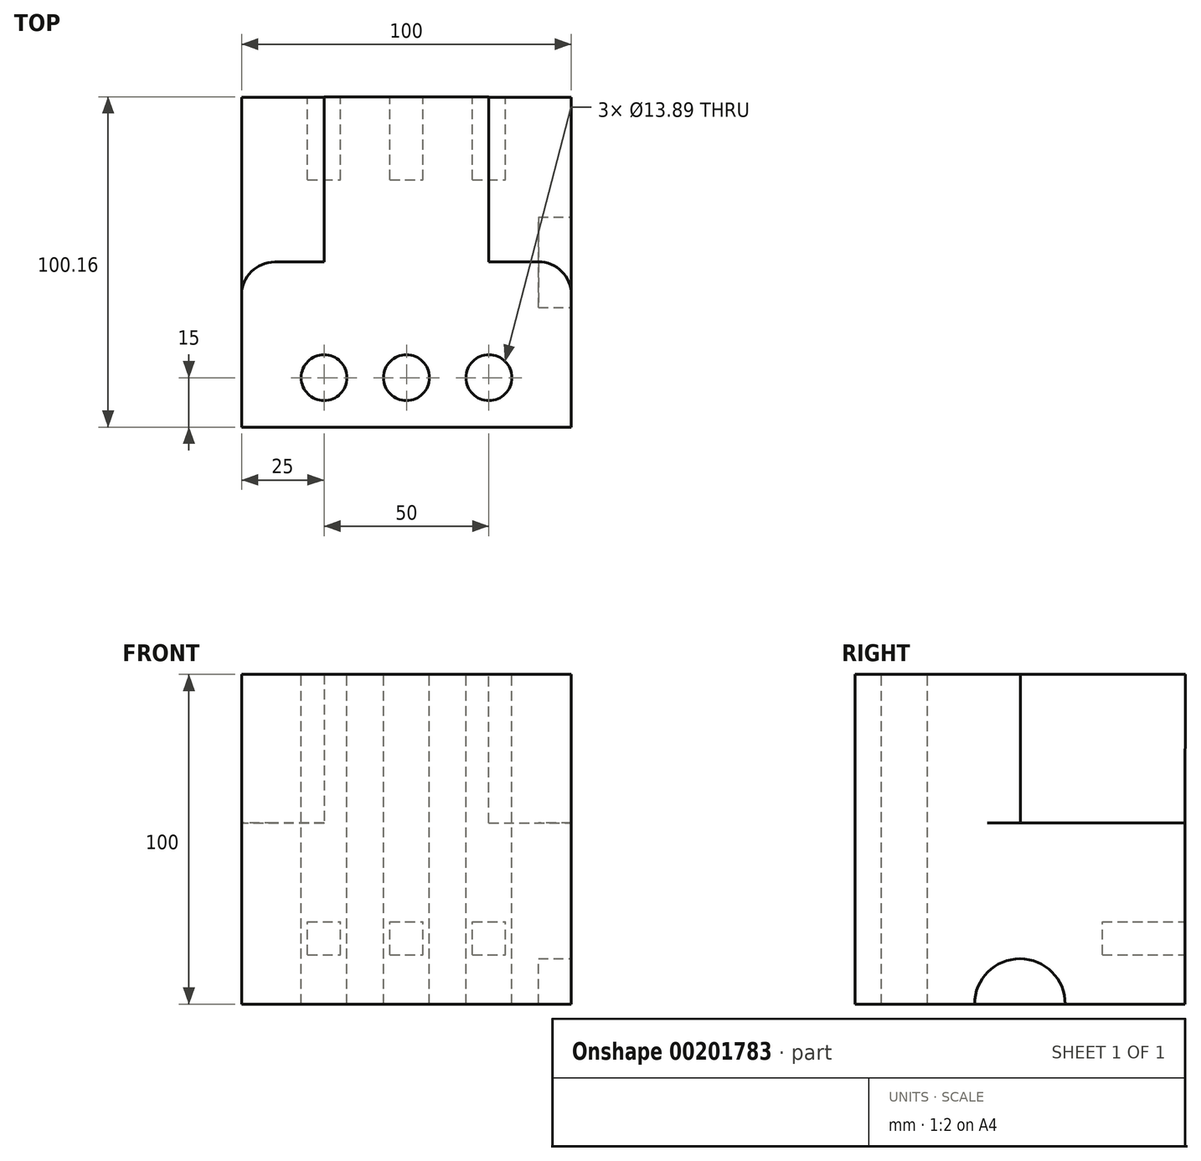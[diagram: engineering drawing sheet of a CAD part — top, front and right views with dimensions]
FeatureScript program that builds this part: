
annotation { "Feature Type Name" : "Feature", "Feature Type Description" : "" }
export const myFeature = defineFeature(function(context is Context, id is Id, definition is map)
    precondition{}
    {
        {
            var Q0;
            Q0=qCreatedBy(makeId("Right.planeOp"),FACE);
            var sketch = newSketch(context, id + "F0", { "sketchPlane" : qUnion([Q0])});
            skLineSegment(sketch, "E0", {"start": v(0, 100) * mm, "end": v(0, 0) * mm});
            skLineSegment(sketch, "E1", {"start": v(0, 0) * mm, "end": v(100, 0) * mm});
            skLineSegment(sketch, "E2", {"start": v(100, 0) * mm, "end": v(100, 55) * mm});
            skLineSegment(sketch, "E3", {"start": v(100, 55) * mm, "end": v(50, 55) * mm});
            skLineSegment(sketch, "E4", {"start": v(50, 55) * mm, "end": v(50, 100) * mm});
            skLineSegment(sketch, "E5", {"start": v(50, 100) * mm, "end": v(0, 100) * mm});
            skArc(sketch, "E6", {"start": v(63.75, 0) * mm, "mid": v(50, 13.75) * mm, "end": v(36.25, 0) * mm});
            skLineSegment(sketch, "E7", {"start": v(50, 100) * mm, "end": v(100.16, 100) * mm});
            skLineSegment(sketch, "E8", {"start": v(100, 55) * mm, "end": v(100.16, 100) * mm});
            skSolve(sketch);
        }
        {
            var Q0;
            Q0 = qSketchRegion(id + "F0", true);
            extrude(context, id + "F1", {"entities" : qUnion([Q0]), "oppositeDirection" : true, "depth" : 100 * mm});
        }
        {
            var Q0;
            {var subQ0=sQuery(id+"F0.wireOp",EDGE,"E6");Q0=makeQuery(id+"F0.imprint","IMPRINT",FACE,{"disambiguationData":[TD([[makeQuery(id+"F0.imprint","IMPRINT",EDGE,{"derivedFrom":subQ0}),1.0]])]});}
            var Q1;
            Q1=sQuery(id+"F0.wireOp",EDGE,"E6");
            extrude(context, id + "F2", {"entities" : qUnion([Q0]), "operationType" : NewBodyOperationType.REMOVE, "surfaceEntities" : qUnion([Q1]), "oppositeDirection" : true, "depth" : 10 * mm});
        }
        {
            var Q0;
            Q0=makeQuery(id+"F1.opExtrude","CAP_FACE",FACE,{"disambiguationData":[OSD([sQuery(id+"F0.wireOp",EDGE,"E0"),sQuery(id+"F0.wireOp",EDGE,"E1"),sQuery(id+"F0.wireOp",EDGE,"E2"),sQuery(id+"F0.wireOp",EDGE,"E5"),sQuery(id+"F0.wireOp",EDGE,"E7"),sQuery(id+"F0.wireOp",EDGE,"E8")])],"isStart":false});
            var sketch = newSketch(context, id + "F3", { "sketchPlane" : qUnion([Q0])});
            skPoint(sketch, "E9.endSnap0", {"position": v(-50.08, 100) * mm});
            skLineSegment(sketch, "E10", {"start": v(-50.08, 100) * mm, "end": v(-50.08, 55) * mm});
            skLineSegment(sketch, "E11", {"start": v(-50.08, 55) * mm, "end": v(-100, 54.83) * mm});
            skSolve(sketch);
        }
        {
            var Q0;
            Q0 = qSketchRegion(id + "F3", true);
            var Q1;
            {var subQ4=sQuery(id+"F3.wireOp",EDGE,"E10");Q1=makeQuery(id+"F3.imprint","IMPRINT",FACE,{"disambiguationData":[TD([[makeQuery(id+"F3.imprint","IMPRINT",EDGE,{"derivedFrom":subQ4}),-1.0]])]});}
            var Q2;
            Q2=qNothing();
            extrude(context, id + "F4", {"entities" : qUnion([Q0, Q1]), "operationType" : NewBodyOperationType.REMOVE, "surfaceEntities" : qUnion([Q2]), "oppositeDirection" : true, "depth" : 25 * mm});
        }
        {
            var Q0;
            Q0=makeQuery(id+"F1.opExtrude","SWEPT_FACE",FACE,{"disambiguationData":[OSD([sQuery(id+"F0.wireOp",EDGE,"E5"),sQuery(id+"F0.wireOp",EDGE,"E7")])]});
            var sketch = newSketch(context, id + "F5", { "sketchPlane" : qUnion([Q0])});
            skLineSegment(sketch, "E12", {"start": v(-100, 0) * mm, "end": v(-100, 40.08) * mm});
            skLineSegment(sketch, "E13", {"start": v(-90, 50.08) * mm, "end": v(-75, 50.08) * mm});
            skLineSegment(sketch, "E14", {"start": v(-75, 100.16) * mm, "end": v(-25, 100.16) * mm});
            skLineSegment(sketch, "E15", {"start": v(-25, 100.16) * mm, "end": v(-25, 50.16) * mm});
            skLineSegment(sketch, "E16", {"start": v(-25, 50.16) * mm, "end": v(-10, 50.16) * mm});
            skLineSegment(sketch, "E17", {"start": v(0, 40.16) * mm, "end": v(0, 0) * mm});
            skLineSegment(sketch, "E18", {"start": v(0, 0) * mm, "end": v(-100, 0) * mm});
            skArc(sketch, "E19.filletArc", {"start": v(-90, 50.08) * mm, "mid": v(-97.07, 47.15) * mm, "end": v(-100, 40.08) * mm});
            skArc(sketch, "E20.filletArc", {"start": v(0, 40.16) * mm, "mid": v(-2.93, 47.23) * mm, "end": v(-10, 50.16) * mm});
            skCircle(sketch, "E21", {"center": v(-75, 15) * mm, "radius": 6.95 * mm});
            skCircle(sketch, "E22.1.0.0", {"center": v(-50, 15) * mm, "radius": 6.95 * mm});
            skCircle(sketch, "E22.2.0.0", {"center": v(-25, 15) * mm, "radius": 6.95 * mm});
            skLineSegment(sketch, "E22.direction1", {"start": v(-75, 15) * mm, "end": v(-50, 15) * mm, "construction": true});
            skLineSegment(sketch, "E23", {"start": v(-75, 100.16) * mm, "end": v(-75, 50.16) * mm});
            skSolve(sketch);
        }
        {
            var Q0;
            {var subQ0=sQuery(id+"F5.wireOp",EDGE,"E20.filletArc");Q0=makeQuery(id+"F5.imprint","IMPRINT",FACE,{"disambiguationData":[TD([[makeQuery(id+"F5.imprint","IMPRINT",EDGE,{"derivedFrom":subQ0}),-1.0]])]});}
            extrude(context, id + "F6", {"entities" : qUnion([Q0]), "operationType" : NewBodyOperationType.REMOVE, "oppositeDirection" : true, "depth" : 45 * mm});
        }
        {
            var Q0;
            {var subQ0=sQuery(id+"F5.wireOp",EDGE,"E19.filletArc");Q0=makeQuery(id+"F5.imprint","IMPRINT",FACE,{"disambiguationData":[TD([[makeQuery(id+"F5.imprint","IMPRINT",EDGE,{"derivedFrom":subQ0}),-1.0]])]});}
            extrude(context, id + "F7", {"entities" : qUnion([Q0]), "operationType" : NewBodyOperationType.REMOVE, "oppositeDirection" : true, "depth" : 45 * mm});
        }
        {
            var Q0;
            Q0=makeQuery(id+"F5.imprint","IMPRINT",FACE,{"disambiguationData":[TD([[makeQuery(id+"F5.imprint","IMPRINT",EDGE,{"derivedFrom":sQuery(id+"F5.wireOp",EDGE,"E21")}),1.0]])]});
            var Q1;
            Q1=makeQuery(id+"F5.imprint","IMPRINT",FACE,{"disambiguationData":[TD([[makeQuery(id+"F5.imprint","IMPRINT",EDGE,{"derivedFrom":sQuery(id+"F5.wireOp",EDGE,"E22.2.0.0")}),1.0]])]});
            var Q2;
            Q2=makeQuery(id+"F5.imprint","IMPRINT",FACE,{"disambiguationData":[TD([[makeQuery(id+"F5.imprint","IMPRINT",EDGE,{"derivedFrom":sQuery(id+"F5.wireOp",EDGE,"E22.1.0.0")}),1.0]])]});
            extrude(context, id + "F8", {"entities" : qUnion([Q0, Q1, Q2]), "operationType" : NewBodyOperationType.REMOVE, "oppositeDirection" : true, "depth" : 100 * mm});
        }
        {
            var Q0;
            Q0=makeQuery(id+"F1.opExtrude","SWEPT_FACE",FACE,{"disambiguationData":[OSD([sQuery(id+"F0.wireOp",EDGE,"E2")])]});
            var sketch = newSketch(context, id + "F9", { "sketchPlane" : qUnion([Q0])});
            skLineSegment(sketch, "E24.bottom", {"start": v(30, 15) * mm, "end": v(20, 15) * mm});
            skLineSegment(sketch, "E24.top", {"start": v(30, 25) * mm, "end": v(20, 25) * mm});
            skLineSegment(sketch, "E24.left", {"start": v(30, 15) * mm, "end": v(30, 25) * mm});
            skLineSegment(sketch, "E24.right", {"start": v(20, 15) * mm, "end": v(20, 25) * mm});
            skPoint(sketch, "E24.middle", {"position": v(25, 20) * mm});
            skLineSegment(sketch, "E25.1.0.0", {"start": v(55, 15) * mm, "end": v(55, 25) * mm});
            skLineSegment(sketch, "E25.1.0.1", {"start": v(55, 25) * mm, "end": v(45, 25) * mm});
            skLineSegment(sketch, "E25.1.0.2", {"start": v(55, 15) * mm, "end": v(45, 15) * mm});
            skLineSegment(sketch, "E25.1.0.3", {"start": v(45, 15) * mm, "end": v(45, 25) * mm});
            skLineSegment(sketch, "E25.2.0.0", {"start": v(80, 15) * mm, "end": v(80, 25) * mm});
            skLineSegment(sketch, "E25.2.0.1", {"start": v(80, 25) * mm, "end": v(70, 25) * mm});
            skLineSegment(sketch, "E25.2.0.2", {"start": v(80, 15) * mm, "end": v(70, 15) * mm});
            skLineSegment(sketch, "E25.2.0.3", {"start": v(70, 15) * mm, "end": v(70, 25) * mm});
            skLineSegment(sketch, "E25.direction1", {"start": v(20, 15) * mm, "end": v(45, 15) * mm, "construction": true});
            skSolve(sketch);
        }
        {
            var Q0;
            Q0=makeQuery(id+"F9.imprint","IMPRINT",FACE,{"disambiguationData":[TD([[makeQuery(id+"F9.imprint","IMPRINT",EDGE,{"derivedFrom":sQuery(id+"F9.wireOp",EDGE,"E25.1.0.0")}),1.0]])]});
            var Q1;
            Q1=makeQuery(id+"F9.imprint","IMPRINT",FACE,{"disambiguationData":[TD([[makeQuery(id+"F9.imprint","IMPRINT",EDGE,{"derivedFrom":sQuery(id+"F9.wireOp",EDGE,"E25.2.0.0")}),1.0]])]});
            var Q2;
            Q2=makeQuery(id+"F9.imprint","IMPRINT",FACE,{"disambiguationData":[TD([[makeQuery(id+"F9.imprint","IMPRINT",EDGE,{"derivedFrom":sQuery(id+"F9.wireOp",EDGE,"E24.bottom")}),-1.0]])]});
            extrude(context, id + "F10", {"entities" : qUnion([Q0, Q1, Q2]), "operationType" : NewBodyOperationType.REMOVE, "oppositeDirection" : true, "depth" : 25 * mm});
        }
    });
